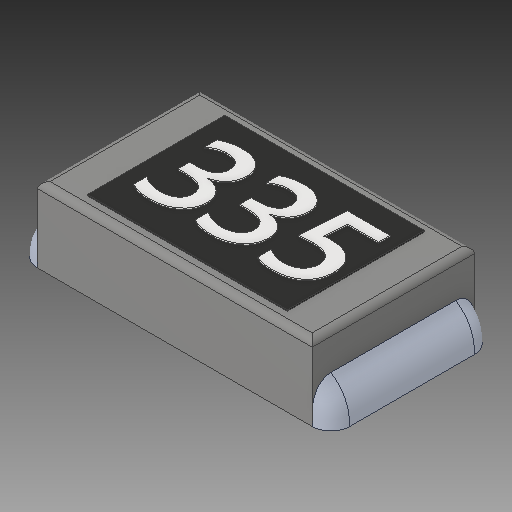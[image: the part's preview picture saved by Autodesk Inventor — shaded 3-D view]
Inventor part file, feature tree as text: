
AUTODESK INVENTOR PART (.ipt)
format: ipt  version: 2018.3 (Build 223284000, 284)  size: 290,816 bytes
history: native  units: mm
features: other x4, fillet x1, mirror x1
ambient origin geometry x8: Origin, YZ Plane, XZ Plane, XY Plane, X Axis, Y Axis, Z Axis, Center Point
bodies: Body1 (feature_tree), Body2 (feature_tree), Body3 (feature_tree)
feature tree (6):
  other  "Sólido1"
  other  "Sólido2"
  other  "Sólido3"
  fillet  "Fillet2"  [1 undecoded]
  mirror  "Mirror1"
  other  "Boss-Extrude4"
note: 1 required parameter value undecoded (feature->parameter linkage not recoverable at this tier; creation-order binding heuristic only, values carry confidence <= 0.55)
